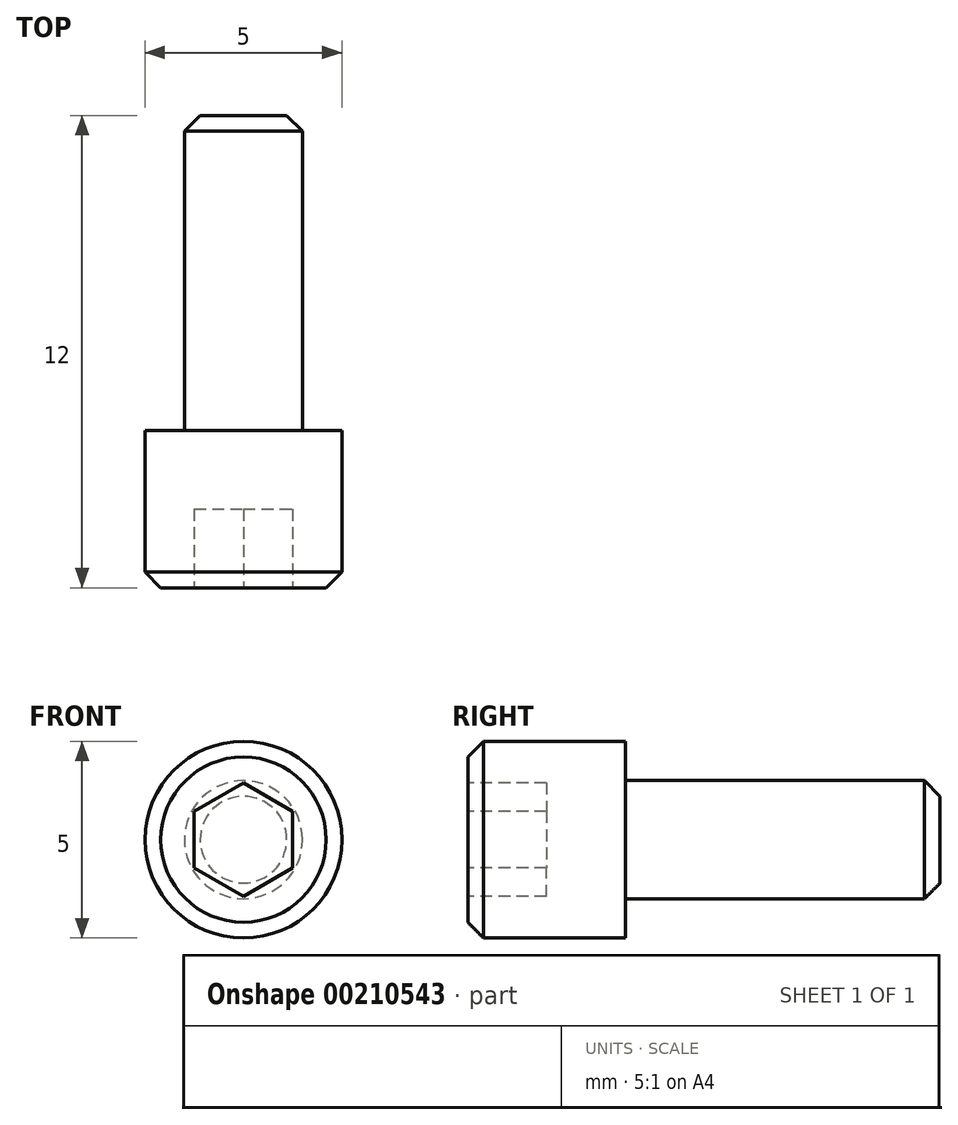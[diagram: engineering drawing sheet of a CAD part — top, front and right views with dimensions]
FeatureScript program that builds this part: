
annotation { "Feature Type Name" : "Feature", "Feature Type Description" : "" }
export const myFeature = defineFeature(function(context is Context, id is Id, definition is map)
    precondition{}
    {
        {
            var Q0;
            Q0=qCreatedBy(makeId("Front.planeOp"),FACE);
            var sketch = newSketch(context, id + "F0", { "sketchPlane" : qUnion([Q0])});
            skCircle(sketch, "E0", {"center": v(0, 0) * mm, "radius": 1.5 * mm});
            skCircle(sketch, "E1", {"center": v(0, 0) * mm, "radius": 2.5 * mm});
            skSolve(sketch);
        }
        {
            var Q0;
            Q0=makeQuery(id+"F0.imprint","IMPRINT",FACE,{"disambiguationData":[TD([[makeQuery(id+"F0.imprint","IMPRINT",EDGE,{"derivedFrom":sQuery(id+"F0.wireOp",EDGE,"E0")}),1.0]])]});
            extrude(context, id + "F1", {"entities" : qUnion([Q0]), "oppositeDirection" : true, "depth" : 8 * mm});
        }
        {
            var Q0;
            Q0=qSketchRegion(id+"FqODLZG30JXXEfw_0",true);
            var Q1;
            Q1=makeQuery(id+"F0.imprint","IMPRINT",FACE,{"disambiguationData":[TD([[makeQuery(id+"F0.imprint","IMPRINT",EDGE,{"derivedFrom":sQuery(id+"F0.wireOp",EDGE,"E0")}),-1.0]])]});
            var Q2;
            Q2=makeQuery(id+"F0.imprint","IMPRINT",FACE,{"disambiguationData":[TD([[makeQuery(id+"F0.imprint","IMPRINT",EDGE,{"derivedFrom":sQuery(id+"F0.wireOp",EDGE,"E0")}),1.0]])]});
            extrude(context, id + "F2", {"entities" : qUnion([Q0, Q1, Q2]), "operationType" : NewBodyOperationType.ADD, "depth" : 4 * mm});
        }
        {
            var Q0;
            Q0=makeQuery(id+"F2.opExtrude","CAP_FACE",FACE,{"disambiguationData":[OSD([sQuery(id+"F0.wireOp",EDGE,"E1")])],"isStart":false});
            var sketch = newSketch(context, id + "F3", { "sketchPlane" : qUnion([Q0])});
            skCircle(sketch, "E2.cCircle", {"center": v(0, 0) * mm, "radius": 1.25 * mm, "construction": true});
            skLineSegment(sketch, "E2.0", {"start": v(1.25, 0.72) * mm, "end": v(1.25, -0.72) * mm});
            skLineSegment(sketch, "E2.1", {"start": v(1.25, -0.72) * mm, "end": v(0, -1.44) * mm});
            skLineSegment(sketch, "E2.2", {"start": v(0, -1.44) * mm, "end": v(-1.25, -0.72) * mm});
            skLineSegment(sketch, "E2.3", {"start": v(-1.25, -0.72) * mm, "end": v(-1.25, 0.72) * mm});
            skLineSegment(sketch, "E2.4", {"start": v(-1.25, 0.72) * mm, "end": v(0, 1.44) * mm});
            skLineSegment(sketch, "E2.5", {"start": v(0, 1.44) * mm, "end": v(1.25, 0.72) * mm});
            skPoint(sketch, "E2.0.midPoint", {"position": v(1.25, 0) * mm});
            skSolve(sketch);
        }
        {
            var Q0;
            Q0=qSketchRegion(id+"F3",true);
            extrude(context, id + "F4", {"entities" : qUnion([Q0]), "operationType" : NewBodyOperationType.REMOVE, "oppositeDirection" : true, "depth" : 2 * mm});
        }
        {
            var Q0;
            Q0=makeQuery(id+"F2.opExtrude","CAP_EDGE",EDGE,{"disambiguationData":[OSD([sQuery(id+"F0.wireOp",EDGE,"E1")])],"isStart":false});
            var Q1;
            Q1=makeQuery(id+"F1.opExtrude","CAP_EDGE",EDGE,{"disambiguationData":[OSD([sQuery(id+"F0.wireOp",EDGE,"E0")])],"isStart":false});
            chamfer(context, id + "F5", {"entities" : qUnion([Q0, Q1]), "width" : .4 * mm, "tangentPropagation" : true});
        }
    });
